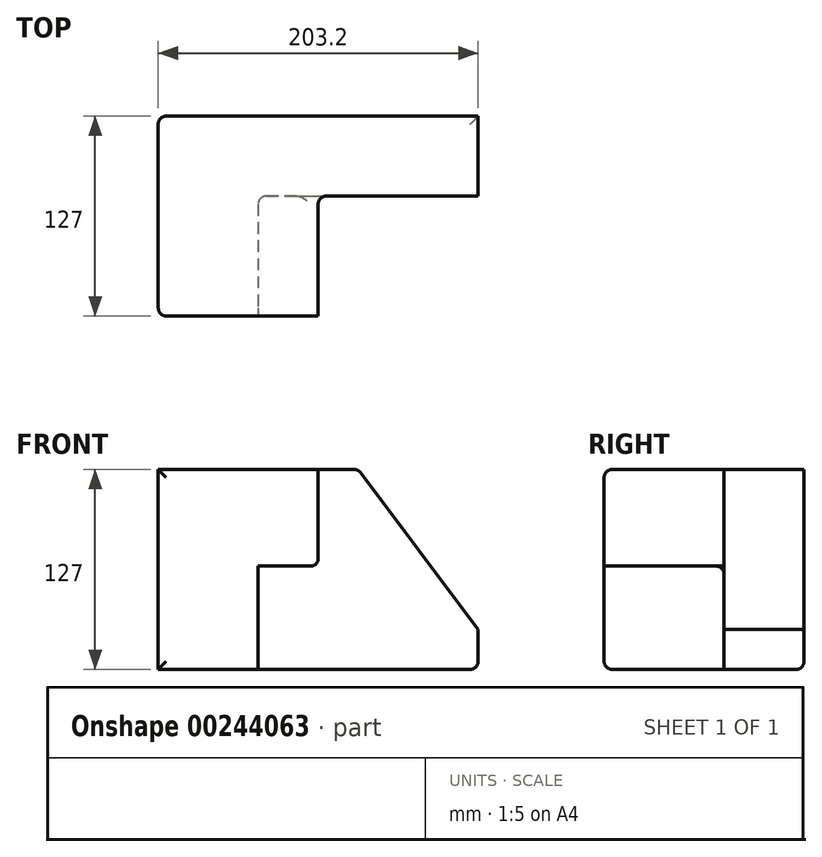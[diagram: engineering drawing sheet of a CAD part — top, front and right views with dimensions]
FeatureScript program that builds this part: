
annotation { "Feature Type Name" : "Feature", "Feature Type Description" : "" }
export const myFeature = defineFeature(function(context is Context, id is Id, definition is map)
    precondition{}
    {
        {
            var Q0;
            Q0=qCreatedBy(makeId("Front.planeOp"),FACE);
            var sketch = newSketch(context, id + "F0", { "sketchPlane" : qUnion([Q0])});
            skLineSegment(sketch, "E0.bottom", {"start": v(-92.78, 57.62) * mm, "end": v(110.42, 57.62) * mm});
            skLineSegment(sketch, "E0.top", {"start": v(-92.78, -69.38) * mm, "end": v(110.42, -69.38) * mm});
            skLineSegment(sketch, "E0.left", {"start": v(-92.78, 57.62) * mm, "end": v(-92.78, -69.38) * mm});
            skLineSegment(sketch, "E0.right", {"start": v(110.42, 57.62) * mm, "end": v(110.42, -69.38) * mm});
            skSolve(sketch);
        }
        {
            var Q0;
            Q0 = qSketchRegion(id + "F0", true);
            extrude(context, id + "F1", {"entities" : qUnion([Q0]), "depth" : 127 * mm});
        }
        {
            var Q0;
            Q0=makeQuery(id+"F1.opExtrude","CAP_FACE",FACE,{"disambiguationData":[OSD([sQuery(id+"F0.wireOp",EDGE,"E0.bottom"),sQuery(id+"F0.wireOp",EDGE,"E0.top"),sQuery(id+"F0.wireOp",EDGE,"E0.left"),sQuery(id+"F0.wireOp",EDGE,"E0.right")])],"isStart":false});
            var sketch = newSketch(context, id + "F2", { "sketchPlane" : qUnion([Q0])});
            skLineSegment(sketch, "E1", {"start": v(8.82, 57.62) * mm, "end": v(8.82, -3.77) * mm});
            skLineSegment(sketch, "E2", {"start": v(8.82, -3.77) * mm, "end": v(-29.28, -3.77) * mm});
            skLineSegment(sketch, "E3", {"start": v(-29.28, -3.77) * mm, "end": v(-29.28, -69.38) * mm});
            skSolve(sketch);
        }
        {
            var Q0;
            {var subQ2=sQuery(id+"F2.wireOp",EDGE,"E1");Q0=makeQuery(id+"F2.imprint","IMPRINT",FACE,{"disambiguationData":[TD([[makeQuery(id+"F2.imprint","IMPRINT",EDGE,{"derivedFrom":subQ2}),1.0]])]});}
            extrude(context, id + "F3", {"entities" : qUnion([Q0]), "operationType" : NewBodyOperationType.REMOVE, "oppositeDirection" : true, "depth" : 76.2 * mm});
        }
        {
            var Q0;
            Q0=makeQuery(id+"F1.opExtrude","SWEPT_EDGE",EDGE,{"disambiguationData":[OSD([sQuery(id+"F0.wireOp",EDGE,"E0.bottom"),sQuery(id+"F0.wireOp",EDGE,"E0.right")])]});
            chamfer(context, id + "F4", {"entities" : qUnion([Q0]), "chamferType" : ChamferType.TWO_OFFSETS, "width1" : 76.2 * mm, "oppositeDirection" : false, "width2" : 101.6 * mm, "tangentPropagation" : true});
        }
        {
            var Q0;
            Q0=makeQuery(id+"F1.opExtrude","CAP_EDGE",EDGE,{"disambiguationData":[OSD([sQuery(id+"F0.wireOp",EDGE,"E0.bottom")])],"isStart":false});
            var Q1;
            Q1=makeQuery(id+"F3.boolean.opBoolean","COPY",EDGE,{"derivedFrom":makeQuery(id+"F3.opExtrude","SWEPT_EDGE",EDGE,{"disambiguationData":[OSD([sQuery(id+"F0.wireOp",EDGE,"E0.bottom"),sQuery(id+"F2.wireOp",EDGE,"E1")])]})});
            var Q2;
            Q2=makeQuery(id+"F3.boolean.opBoolean","COPY",EDGE,{"derivedFrom":makeQuery(id+"F3.opExtrude","CAP_EDGE",EDGE,{"disambiguationData":[OSD([sQuery(id+"F0.wireOp",EDGE,"E0.bottom")])],"isStart":false})});
            var Q3;
            {var subQ0=sQuery(id+"F0.wireOp",EDGE,"E0.bottom");Q3=makeQuery(id+"F4.opChamfer","BLEND_EDGE",EDGE,{"blendedFrom":[makeQuery(id+"F1.opExtrude","SWEPT_EDGE",EDGE,{"disambiguationData":[OSD([subQ0,sQuery(id+"F0.wireOp",EDGE,"E0.right")])]}),makeQuery(id+"F1.opExtrude","SWEPT_FACE",FACE,{"disambiguationData":[OSD([subQ0])]})],"blendedInto":[makeQuery(id+"F1.opExtrude","SWEPT_FACE",FACE,{"disambiguationData":[OSD([subQ0])]})]});}
            var Q4;
            Q4=makeQuery(id+"F3.boolean.opBoolean","COPY",EDGE,{"derivedFrom":makeQuery(id+"F3.opExtrude","CAP_EDGE",EDGE,{"disambiguationData":[OSD([sQuery(id+"F2.wireOp",EDGE,"E1")])],"isStart":false})});
            var Q5;
            Q5=makeQuery(id+"F3.boolean.opBoolean","COPY",EDGE,{"derivedFrom":makeQuery(id+"F3.opExtrude","CAP_EDGE",EDGE,{"disambiguationData":[OSD([sQuery(id+"F2.wireOp",EDGE,"E1")])],"isStart":true})});
            var Q6;
            Q6=makeQuery(id+"F3.boolean.opBoolean","COPY",EDGE,{"derivedFrom":makeQuery(id+"F3.opExtrude","CAP_EDGE",EDGE,{"disambiguationData":[OSD([sQuery(id+"F2.wireOp",EDGE,"E2")])],"isStart":true})});
            var Q7;
            Q7=makeQuery(id+"F3.boolean.opBoolean","COPY",EDGE,{"derivedFrom":makeQuery(id+"F3.opExtrude","SWEPT_EDGE",EDGE,{"disambiguationData":[OSD([sQuery(id+"F2.wireOp",EDGE,"E1"),sQuery(id+"F2.wireOp",EDGE,"E2")])]})});
            var Q8;
            Q8=makeQuery(id+"F3.boolean.opBoolean","COPY",EDGE,{"derivedFrom":makeQuery(id+"F3.opExtrude","CAP_EDGE",EDGE,{"disambiguationData":[OSD([sQuery(id+"F2.wireOp",EDGE,"E3")])],"isStart":true})});
            var Q9;
            Q9=makeQuery(id+"F3.boolean.opBoolean","COPY",EDGE,{"derivedFrom":makeQuery(id+"F3.opExtrude","CAP_EDGE",EDGE,{"disambiguationData":[OSD([sQuery(id+"F2.wireOp",EDGE,"E3")])],"isStart":false})});
            var Q10;
            Q10=makeQuery(id+"F1.opExtrude","CAP_EDGE",EDGE,{"disambiguationData":[OSD([sQuery(id+"F0.wireOp",EDGE,"E0.top")])],"isStart":false});
            var Q11;
            Q11=makeQuery(id+"F3.boolean.opBoolean","COPY",EDGE,{"derivedFrom":makeQuery(id+"F3.opExtrude","SWEPT_EDGE",EDGE,{"disambiguationData":[OSD([sQuery(id+"F0.wireOp",EDGE,"E0.top"),sQuery(id+"F2.wireOp",EDGE,"E3")])]})});
            var Q12;
            Q12=makeQuery(id+"F3.boolean.opBoolean","COPY",EDGE,{"derivedFrom":makeQuery(id+"F3.opExtrude","CAP_EDGE",EDGE,{"disambiguationData":[OSD([sQuery(id+"F0.wireOp",EDGE,"E0.top")])],"isStart":false})});
            var Q13;
            Q13=makeQuery(id+"F1.opExtrude","SWEPT_EDGE",EDGE,{"disambiguationData":[OSD([sQuery(id+"F0.wireOp",EDGE,"E0.top"),sQuery(id+"F0.wireOp",EDGE,"E0.right")])]});
            var Q14;
            Q14=makeQuery(id+"F1.opExtrude","CAP_EDGE",EDGE,{"disambiguationData":[OSD([sQuery(id+"F0.wireOp",EDGE,"E0.left")])],"isStart":false});
            var Q15;
            Q15=makeQuery(id+"F1.opExtrude","CAP_EDGE",EDGE,{"disambiguationData":[OSD([sQuery(id+"F0.wireOp",EDGE,"E0.top")])],"isStart":true});
            var Q16;
            Q16=makeQuery(id+"F1.opExtrude","CAP_EDGE",EDGE,{"disambiguationData":[OSD([sQuery(id+"F0.wireOp",EDGE,"E0.left")])],"isStart":true});
            fillet(context, id + "F5", {"entities" : qUnion([Q0, Q1, Q2, Q3, Q4, Q5, Q6, Q7, Q8, Q9, Q10, Q11, Q12, Q13, Q14, Q15, Q16]), "radius" : 5.08 * mm, "tangentPropagation" : true, "allowEdgeOverflow" : false});
        }
    });
